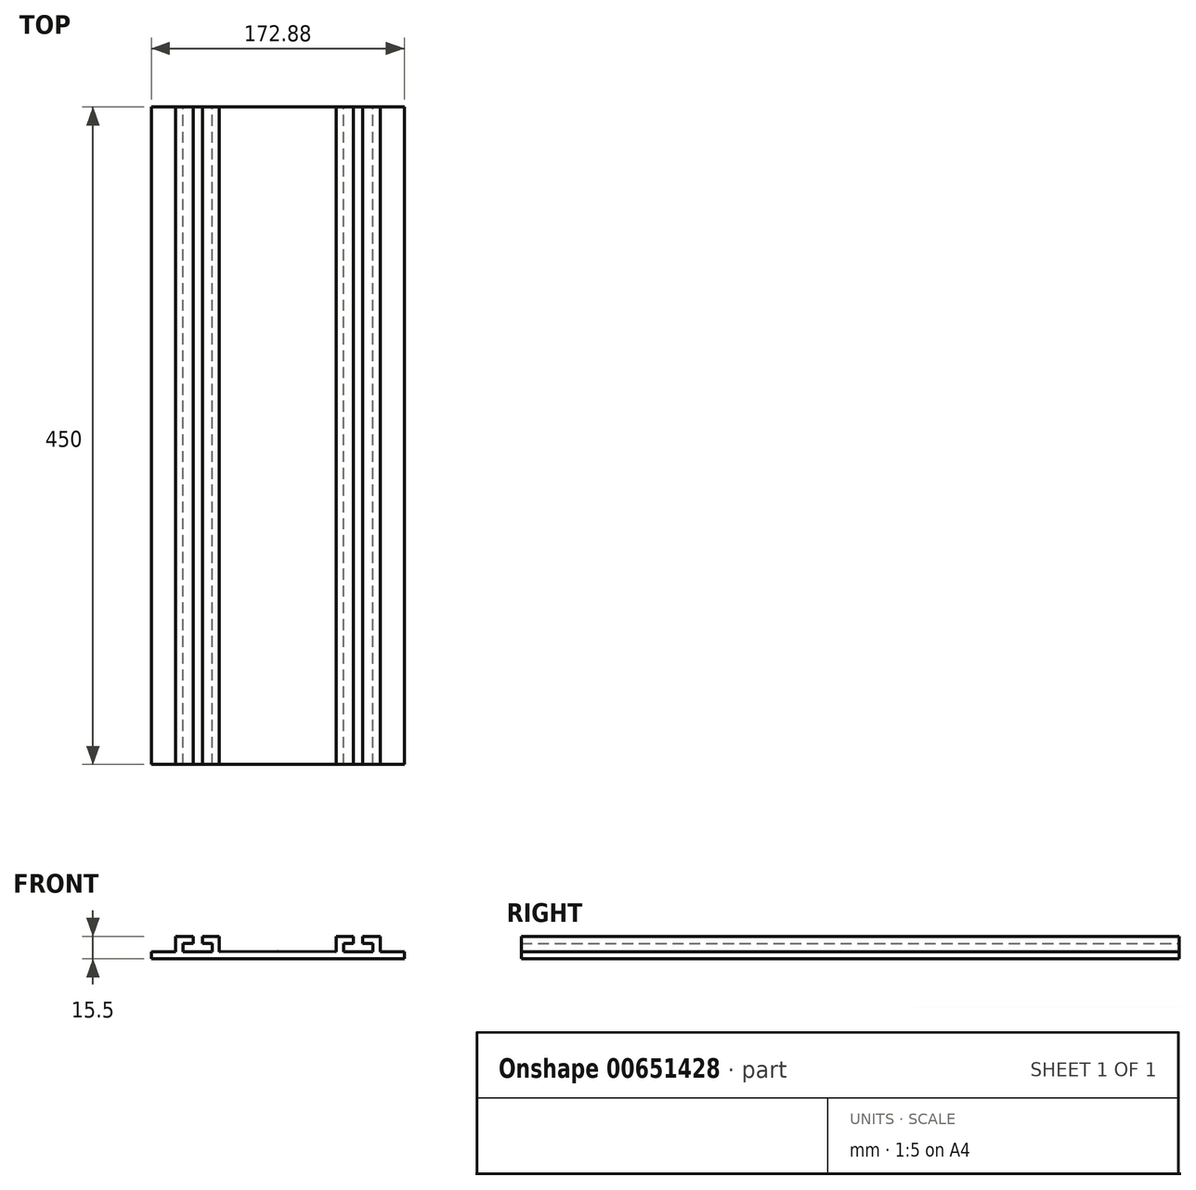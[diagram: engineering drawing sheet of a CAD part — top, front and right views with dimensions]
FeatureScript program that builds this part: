
annotation { "Feature Type Name" : "Feature", "Feature Type Description" : "" }
export const myFeature = defineFeature(function(context is Context, id is Id, definition is map)
    precondition{}
    {
        {
            var Q0;
            Q0=qCreatedBy(makeId("Front.planeOp"),FACE);
            var sketch = newSketch(context, id + "F0", { "sketchPlane" : qUnion([Q0])});
            skLineSegment(sketch, "E0", {"start": v(0, 0) * mm, "end": v(86.44, 0) * mm});
            skLineSegment(sketch, "E1", {"start": v(86.44, 0) * mm, "end": v(86.44, 5) * mm});
            skLineSegment(sketch, "E2", {"start": v(70, 15.5) * mm, "end": v(58, 15.5) * mm});
            skLineSegment(sketch, "E3", {"start": v(58, 15.5) * mm, "end": v(58, 10.5) * mm});
            skLineSegment(sketch, "E4", {"start": v(58, 10.5) * mm, "end": v(65, 10.5) * mm});
            skLineSegment(sketch, "E5", {"start": v(65, 10.5) * mm, "end": v(65, 5) * mm});
            skLineSegment(sketch, "E6", {"start": v(40, 15.5) * mm, "end": v(51.5, 15.5) * mm});
            skLineSegment(sketch, "E7", {"start": v(51.5, 15.5) * mm, "end": v(51.5, 10.5) * mm});
            skLineSegment(sketch, "E8", {"start": v(51.5, 10.5) * mm, "end": v(45, 10.5) * mm});
            skLineSegment(sketch, "E9", {"start": v(45, 10.5) * mm, "end": v(45, 5) * mm});
            skLineSegment(sketch, "E10", {"start": v(40, 15.5) * mm, "end": v(40, 5) * mm});
            skLineSegment(sketch, "E11", {"start": v(70, 15.5) * mm, "end": v(70, 5) * mm});
            skLineSegment(sketch, "E12", {"start": v(0, 5.08) * mm, "end": v(40, 5) * mm});
            skLineSegment(sketch, "E13", {"start": v(45, 5) * mm, "end": v(65, 5) * mm});
            skLineSegment(sketch, "E14", {"start": v(70, 5) * mm, "end": v(86.44, 5) * mm});
            skLineSegment(sketch, "E15.MirrorCS", {"start": v(-86.44, 0) * mm, "end": v(-86.44, 5) * mm});
            skLineSegment(sketch, "E16.MirrorCS", {"start": v(-70, 5) * mm, "end": v(-86.44, 5) * mm});
            skLineSegment(sketch, "E17.MirrorCS", {"start": v(0, 0) * mm, "end": v(-86.44, 0) * mm});
            skLineSegment(sketch, "E18.MirrorCS", {"start": v(-70, 15.5) * mm, "end": v(-70, 5) * mm});
            skLineSegment(sketch, "E19.MirrorCS", {"start": v(-70, 15.5) * mm, "end": v(-58, 15.5) * mm});
            skLineSegment(sketch, "E20.MirrorCS", {"start": v(-58, 15.5) * mm, "end": v(-58, 10.5) * mm});
            skLineSegment(sketch, "E21.MirrorCS", {"start": v(-58, 10.5) * mm, "end": v(-65, 10.5) * mm});
            skLineSegment(sketch, "E22.MirrorCS", {"start": v(-65, 10.5) * mm, "end": v(-65, 5) * mm});
            skLineSegment(sketch, "E23.MirrorCS", {"start": v(-45, 5) * mm, "end": v(-65, 5) * mm});
            skLineSegment(sketch, "E24.MirrorCS", {"start": v(-45, 10.5) * mm, "end": v(-45, 5) * mm});
            skLineSegment(sketch, "E25.MirrorCS", {"start": v(-51.5, 10.5) * mm, "end": v(-45, 10.5) * mm});
            skLineSegment(sketch, "E26.MirrorCS", {"start": v(-51.5, 15.5) * mm, "end": v(-51.5, 10.5) * mm});
            skLineSegment(sketch, "E27.MirrorCS", {"start": v(-40, 15.5) * mm, "end": v(-51.5, 15.5) * mm});
            skLineSegment(sketch, "E28.MirrorCS", {"start": v(-40, 15.5) * mm, "end": v(-40, 5) * mm});
            skLineSegment(sketch, "E29.MirrorCS", {"start": v(0, 5.08) * mm, "end": v(-40, 5) * mm});
            skSolve(sketch);
        }
        {
            var Q0;
            Q0 = qSketchRegion(id + "F0", true);
            extrude(context, id + "F1", {"entities" : qUnion([Q0]), "depth" : 450 * mm, "offsetDistance" : 25 * mm});
        }
    });
